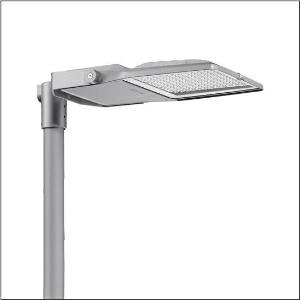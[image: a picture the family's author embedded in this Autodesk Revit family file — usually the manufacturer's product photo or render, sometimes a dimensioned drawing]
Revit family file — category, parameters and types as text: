
# Revit family: floodlight_fl_21_iq_midi___pl33t_5xa7782e4f3a_344b
name_source: partatom
category: Lighting Fixtures
units: mm (PartAtom-declared; Revit-internal decimal feet)

## family parameters
Cut with Voids When Loaded = No
Host = Face
Light Source = No
Part Type = Normal
Room Calculation Point = No
Round Connector Dimension = Use Diameter
Shared = No

## types (1)
- --- (1 x LED, 27690 lm, 208.1 W, 4000K)
    Apparent Load = 208 VA
    CIE Flux Codes = 26 75 99 100 100
    Color Rendering = 70
    Color Temperature = 4000K
    Default Elevation = 1800 mm
    Description = Floodlight FL 21 iQ midi, floodlight, primary light control with lens, of PMMA, primary optical cover: protective disc, of toughened safety glass, transparent, light distribution: PL33T, light emission: direct distribution, installation type: surface-mounted, LED, High Power LED, rated luminous flux: 27.690lm, luminous efficacy: 133lm/W, light colour: 740, colour temperature: 4000K, control gear: ECG iQ, control: optimised constant luminous flux control (CLO 2.0), Desk-Remote (wireless, voltage-free reading and setting of iQ features in the workshop via application-optimized NFC function/RFID function), Smart-Wire, Night-Set, Temp-Guard, Auto-Match, Street-Remote, with terminal, 6-pole, mains connection: 220..240V, AC, 50/60Hz, start of lifetime: 208W, end of service life: 227W, reduction: 90W, luminaire housing, of diecast aluminium, powder-coated, Siteco® metallic grey (DB 702S), corrosivity category C5 mid according to DIN EN ISO 12944, sealing non-destructively replaceable, please order mast flange separately, mast bracket, of steel, galvanised, powder-coated, Siteco® metallic grey (DB 702S), protection rating (complete): IP66, insulation class (complete): insulation class II (safety insulation), certification: CE, protection symbol: D, impact resistance: IK08, permissible operating ambient temperature: -40..+40°C, permissible operating ambient temperature for outdoor applications: -40..+50°C, standard: DIN EN 12944, LABS conformity tested according to VDMA 24364:2018-05, packaging unit: 1 piece

Light Distribution: PL33T
    Height = 76 mm
    Lamp = 1 x LED
    Lamp Light Flux = 27690 lm
    Lamp Power = 208.1 W
    Lamp count = 1
    Length = 657 mm
    Luminous efficacy = 133 lm/W
    Manufacturer = Siteco
    ModVariant = No
    Model = 5XA7782E4F3A
    Number of Poles = 1
    OnlyDefault = Yes
    Power Factor = 1
    Product Name = Floodlight FL 21 iQ midi | PL33T
    Product group = floodlight | pylon annexe
    ProductGroupID = 6200
    Protection Class = Protection class II
    Protection Degree = IP 66
    RLX_Detail_Level = 1
    RLX_Emergency_Light_Flux = 0 lm
    RLX_Emergency_Type = 0
    RLX_Emergency_Type_DB = No
    RlxData = <blob elided: 153513 chars, md5=b64f7958>
    Socket = socket
    Standby Power = 0 W
    System Light Flux = 27690 lm
    System Power = 208 W
    Type Comments = factory setting: luminous flux: 100 % | dim-lin: 254 | 710 mA
    Type Image = l_1007123.jpg
    URL = http://relux.com
    VarID = @adj_052001
    Voltage = 0 V
    Weight = 0.00 kg
    Width = 442 mm

## geometry (parser evidence)
native form markers: Blend x4, Sweep x16
no freeform markers — native parametric forms only
